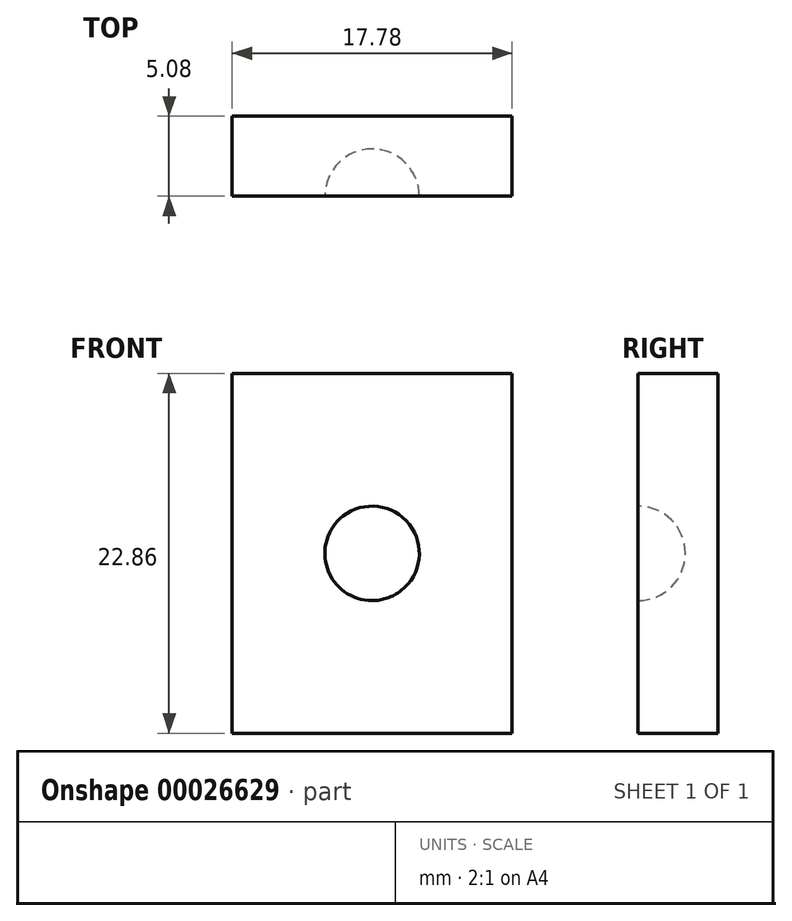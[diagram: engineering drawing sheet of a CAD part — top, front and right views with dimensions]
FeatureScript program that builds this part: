
annotation { "Feature Type Name" : "Feature", "Feature Type Description" : "" }
export const myFeature = defineFeature(function(context is Context, id is Id, definition is map)
    precondition{}
    {
        {
            var Q0;
            Q0=qCreatedBy(makeId("Front.planeOp"),FACE);
            var sketch = newSketch(context, id + "F0", { "sketchPlane" : qUnion([Q0])});
            skLineSegment(sketch, "E0.bottom", {"start": v(-4.41, 3.49) * mm, "end": v(13.37, 3.49) * mm});
            skLineSegment(sketch, "E0.top", {"start": v(-4.41, -19.37) * mm, "end": v(13.37, -19.37) * mm});
            skLineSegment(sketch, "E0.left", {"start": v(-4.41, 3.49) * mm, "end": v(-4.41, -19.37) * mm});
            skLineSegment(sketch, "E0.right", {"start": v(13.37, 3.49) * mm, "end": v(13.37, -19.37) * mm});
            skLineSegment(sketch, "E1", {"start": v(-4.41, 3.49) * mm, "end": v(13.37, -19.37) * mm});
            skCircle(sketch, "E2", {"center": v(4.48, -7.94) * mm, "radius": 4.5 * mm});
            skSolve(sketch);
        }
        {
            var Q0;
            Q0=makeQuery(id+"F0.imprint","IMPRINT",FACE,{"disambiguationData":[TD([[makeQuery(id+"F0.imprint","IMPRINT",EDGE,{"derivedFrom":sQuery(id+"F0.wireOp",EDGE,"E0.bottom")}),-1.0]])]});
            var Q1;
            {var subQ4=sQuery(id+"F0.wireOp",EDGE,"E0.top");Q1=makeQuery(id+"F0.imprint","IMPRINT",FACE,{"disambiguationData":[TD([[makeQuery(id+"F0.imprint","IMPRINT",EDGE,{"derivedFrom":subQ4}),1.0]])]});}
            var Q2;
            {var subQ0=sQuery(id+"F0.wireOp",EDGE,"E2");var subQ1=sQuery(id+"F0.wireOp",EDGE,"E1");var subQ3=makeQuery(id+"F0.imprint","INTERSECT",VERTEX,{"disambiguationData":[OD(0.0)],"derivedFrom":[subQ1,subQ0]});Q2=makeQuery(id+"F0.imprint","IMPRINT",FACE,{"disambiguationData":[TD([[makeQuery(id+"F0.imprint","IMPRINT",EDGE,{"disambiguationData":[TD([[subQ3,-1.0]])],"derivedFrom":subQ1}),1.0]])]});}
            var Q3;
            {var subQ0=sQuery(id+"F0.wireOp",EDGE,"E2");var subQ1=sQuery(id+"F0.wireOp",EDGE,"E1");var subQ3=makeQuery(id+"F0.imprint","INTERSECT",VERTEX,{"disambiguationData":[OD(0.0)],"derivedFrom":[subQ1,subQ0]});Q3=makeQuery(id+"F0.imprint","IMPRINT",FACE,{"disambiguationData":[TD([[makeQuery(id+"F0.imprint","IMPRINT",EDGE,{"disambiguationData":[TD([[subQ3,-1.0]])],"derivedFrom":subQ1}),-1.0]])]});}
            extrude(context, id + "F1", {"entities" : qUnion([Q0, Q1, Q2, Q3]), "depth" : 5.08 * mm});
        }
        {
            var Q0;
            Q0=makeQuery(id+"F1.opExtrude","CAP_FACE",FACE,{"disambiguationData":[OSD([sQuery(id+"F0.wireOp",EDGE,"E0.bottom"),sQuery(id+"F0.wireOp",EDGE,"E0.top"),sQuery(id+"F0.wireOp",EDGE,"E0.left"),sQuery(id+"F0.wireOp",EDGE,"E0.right")])],"isStart":false});
            var sketch = newSketch(context, id + "F2", { "sketchPlane" : qUnion([Q0])});
            skLineSegment(sketch, "E3", {"start": v(13.37, -19.37) * mm, "end": v(-4.41, 3.49) * mm});
            skCircle(sketch, "E4", {"center": v(4.48, -7.94) * mm, "radius": 3 * mm});
            skSolve(sketch);
        }
        {
            var Q0;
            {var subQ0=sQuery(id+"F2.wireOp",EDGE,"E4");var subQ1=sQuery(id+"F2.wireOp",EDGE,"E3");var subQ3=makeQuery(id+"F2.imprint","INTERSECT",VERTEX,{"disambiguationData":[OD(0.0)],"derivedFrom":[subQ1,subQ0]});Q0=makeQuery(id+"F2.imprint","IMPRINT",FACE,{"disambiguationData":[TD([[makeQuery(id+"F2.imprint","IMPRINT",EDGE,{"disambiguationData":[TD([[subQ3,-1.0]])],"derivedFrom":subQ1}),-1.0]])]});}
            var Q1;
            Q1=sQuery(id+"F2.wireOp",EDGE,"E3");
            revolve(context, id + "F3", {"operationType" : NewBodyOperationType.REMOVE, "entities" : qUnion([Q0]), "axis" : qUnion([Q1]), "revolveType" : RevolveType.FULL});
        }
    });
